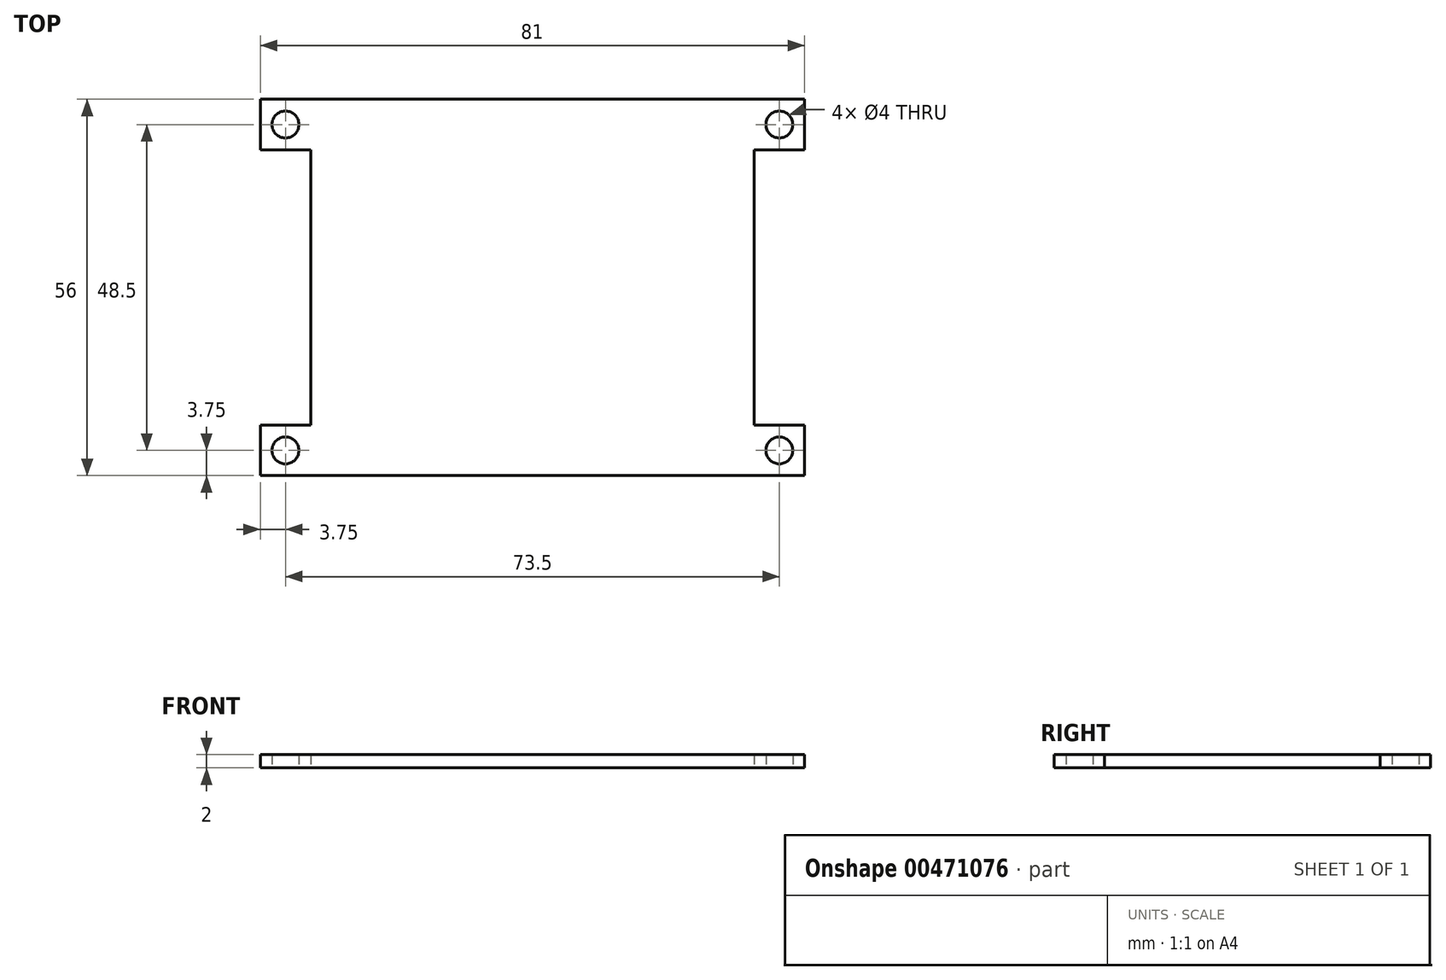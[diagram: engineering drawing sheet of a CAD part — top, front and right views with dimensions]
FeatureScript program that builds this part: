
annotation { "Feature Type Name" : "Feature", "Feature Type Description" : "" }
export const myFeature = defineFeature(function(context is Context, id is Id, definition is map)
    precondition{}
    {
        {
            var Q0;
            Q0=qCreatedBy(makeId("Top.planeOp"),FACE);
            var sketch = newSketch(context, id + "F0", { "sketchPlane" : qUnion([Q0])});
            skLineSegment(sketch, "E0", {"start": v(-51.53, 0) * mm, "end": v(56.23, 0) * mm, "construction": true});
            skLineSegment(sketch, "E1", {"start": v(0, -35.57) * mm, "end": v(0, 33.46) * mm, "construction": true});
            skLineSegment(sketch, "E2", {"start": v(-33, 0) * mm, "end": v(-33, -20.5) * mm});
            skLineSegment(sketch, "E3", {"start": v(-33, -20.5) * mm, "end": v(-40.5, -20.5) * mm});
            skLineSegment(sketch, "E4", {"start": v(-40.5, -20.5) * mm, "end": v(-40.5, -28) * mm});
            skLineSegment(sketch, "E5", {"start": v(-40.5, -28) * mm, "end": v(40.5, -28) * mm});
            skLineSegment(sketch, "E6", {"start": v(40.5, -28) * mm, "end": v(40.5, -20.5) * mm});
            skLineSegment(sketch, "E7", {"start": v(40.5, -20.5) * mm, "end": v(33, -20.5) * mm});
            skLineSegment(sketch, "E8", {"start": v(33, -20.5) * mm, "end": v(33, 0) * mm});
            skCircle(sketch, "E9", {"center": v(36.75, -24.25) * mm, "radius": 2 * mm});
            skPoint(sketch, "E9.centerSnap0", {"position": v(36.75, -20.5) * mm});
            skPoint(sketch, "E9.centerSnap1", {"position": v(40.5, -24.25) * mm});
            skCircle(sketch, "E10", {"center": v(-36.75, -24.25) * mm, "radius": 2 * mm});
            skPoint(sketch, "E10.centerSnap0", {"position": v(-36.75, -20.5) * mm});
            skPoint(sketch, "E10.centerSnap1", {"position": v(-40.5, -24.25) * mm});
            skLineSegment(sketch, "E11.MirrorCS", {"start": v(-33, 0) * mm, "end": v(-33, 20.5) * mm});
            skLineSegment(sketch, "E12.MirrorCS", {"start": v(-33, 20.5) * mm, "end": v(-40.5, 20.5) * mm});
            skLineSegment(sketch, "E13.MirrorCS", {"start": v(-40.5, 20.5) * mm, "end": v(-40.5, 28) * mm});
            skLineSegment(sketch, "E14.MirrorCS", {"start": v(-40.5, 28) * mm, "end": v(40.5, 28) * mm});
            skLineSegment(sketch, "E15.MirrorCS", {"start": v(40.5, 28) * mm, "end": v(40.5, 20.5) * mm});
            skLineSegment(sketch, "E16.MirrorCS", {"start": v(40.5, 20.5) * mm, "end": v(33, 20.5) * mm});
            skLineSegment(sketch, "E17.MirrorCS", {"start": v(33, 20.5) * mm, "end": v(33, 0) * mm});
            skCircle(sketch, "E18.MirrorC", {"center": v(36.75, 24.25) * mm, "radius": 2 * mm});
            skCircle(sketch, "E19.MirrorC", {"center": v(-36.75, 24.25) * mm, "radius": 2 * mm});
            skSolve(sketch);
        }
        {
            var Q0;
            Q0=makeQuery(id+"F0.imprint","IMPRINT",FACE,{"disambiguationData":[TD([[makeQuery(id+"F0.imprint","IMPRINT",EDGE,{"derivedFrom":sQuery(id+"F0.wireOp",EDGE,"E2")}),1.0]])]});
            extrude(context, id + "F1", {"entities" : qUnion([Q0]), "depth" : 2 * mm});
        }
    });
